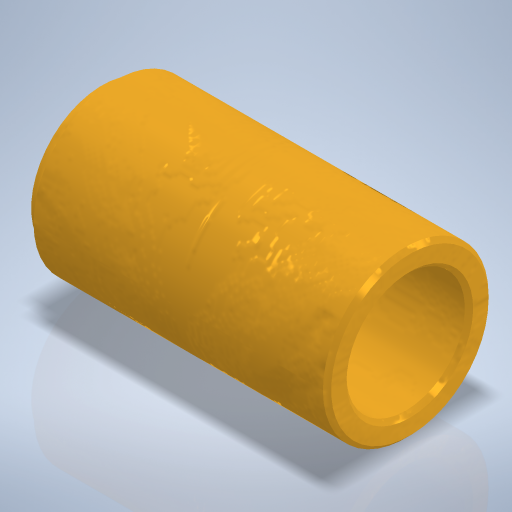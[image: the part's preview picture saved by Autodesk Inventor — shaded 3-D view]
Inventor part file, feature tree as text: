
AUTODESK INVENTOR PART (.ipt)
format: ipt  version: 2024 (Build 280153000, 153)  size: 297,472 bytes
history: native  units: mm
features: sketch x2, revolve x1, extrude x1, chamfer x1
ambient origin geometry x8: Origin, YZ Plane, XZ Plane, XY Plane, X Axis, Y Axis, Z Axis, Center Point
bodies: Volumenkörper1 (feature_tree)
feature tree (5):
  revolve  "Umdrehung1"
  extrude  "Extrusion1"  Depth=26.0mm
  chamfer  "Fasen1"  Distance=1.2mm
  sketch  "Skizze2"  dims[d0=26.0mm d1=14.0mm]
  sketch  "Skizze3"  dims[d2=12.0mm d3=1.2mm d4=90.0deg d5=10.0mm d6=10.0mm d7=0.0mm d8=0.35mm d9=2.0mm d10=45.0deg]
